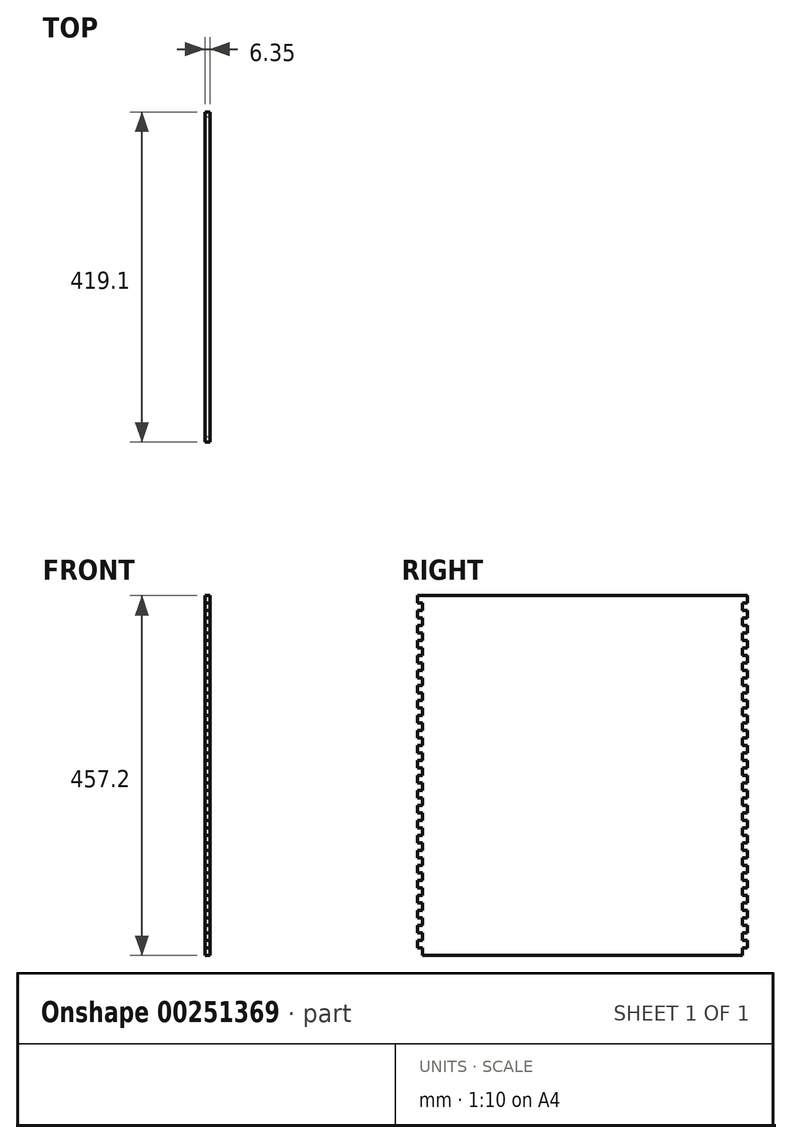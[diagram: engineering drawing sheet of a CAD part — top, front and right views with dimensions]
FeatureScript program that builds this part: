
annotation { "Feature Type Name" : "Feature", "Feature Type Description" : "" }
export const myFeature = defineFeature(function(context is Context, id is Id, definition is map)
    precondition{}
    {
        {
            var Q0;
            Q0=qCreatedBy(makeId("Right.planeOp"),FACE);
            var sketch = newSketch(context, id + "F0", { "sketchPlane" : qUnion([Q0])});
            skLineSegment(sketch, "E0.bottom", {"start": v(-209.55, 228.6) * mm, "end": v(209.55, 228.6) * mm});
            skLineSegment(sketch, "E0.top", {"start": v(-203.2, -228.6) * mm, "end": v(203.2, -228.6) * mm});
            skPoint(sketch, "E0.middle", {"position": v(0, 0) * mm});
            skLineSegment(sketch, "E1.top", {"start": v(-209.55, -219.08) * mm, "end": v(-203.2, -219.08) * mm});
            skLineSegment(sketch, "E1.right", {"start": v(-203.2, -228.6) * mm, "end": v(-203.2, -219.08) * mm});
            skPoint(sketch, "E2.orphan", {"position": v(-215.9, -228.6) * mm});
            skLineSegment(sketch, "E3", {"start": v(-209.55, -219.08) * mm, "end": v(-209.55, -209.55) * mm});
            skLineSegment(sketch, "E4", {"start": v(-209.55, -209.55) * mm, "end": v(-203.2, -209.55) * mm});
            skLineSegment(sketch, "E5.0.1.0", {"start": v(-209.55, -190.5) * mm, "end": v(-203.2, -190.5) * mm});
            skLineSegment(sketch, "E5.0.1.1", {"start": v(-209.55, -200.03) * mm, "end": v(-209.55, -190.5) * mm});
            skLineSegment(sketch, "E5.0.1.2", {"start": v(-209.55, -200.03) * mm, "end": v(-203.2, -200.03) * mm});
            skLineSegment(sketch, "E5.0.1.3", {"start": v(-203.2, -209.55) * mm, "end": v(-203.2, -200.03) * mm});
            skLineSegment(sketch, "E5.0.2.0", {"start": v(-209.55, -171.45) * mm, "end": v(-203.2, -171.45) * mm});
            skLineSegment(sketch, "E5.0.2.1", {"start": v(-209.55, -180.98) * mm, "end": v(-209.55, -171.45) * mm});
            skLineSegment(sketch, "E5.0.2.2", {"start": v(-209.55, -180.97) * mm, "end": v(-203.2, -180.97) * mm});
            skLineSegment(sketch, "E5.0.2.3", {"start": v(-203.2, -190.5) * mm, "end": v(-203.2, -180.98) * mm});
            skLineSegment(sketch, "E5.0.3.0", {"start": v(-209.55, -152.4) * mm, "end": v(-203.2, -152.4) * mm});
            skLineSegment(sketch, "E5.0.3.1", {"start": v(-209.55, -161.93) * mm, "end": v(-209.55, -152.4) * mm});
            skLineSegment(sketch, "E5.0.3.2", {"start": v(-209.55, -161.92) * mm, "end": v(-203.2, -161.92) * mm});
            skLineSegment(sketch, "E5.0.3.3", {"start": v(-203.2, -171.45) * mm, "end": v(-203.2, -161.93) * mm});
            skLineSegment(sketch, "E5.0.4.0", {"start": v(-209.55, -133.35) * mm, "end": v(-203.2, -133.35) * mm});
            skLineSegment(sketch, "E5.0.4.1", {"start": v(-209.55, -142.88) * mm, "end": v(-209.55, -133.35) * mm});
            skLineSegment(sketch, "E5.0.4.2", {"start": v(-209.55, -142.87) * mm, "end": v(-203.2, -142.87) * mm});
            skLineSegment(sketch, "E5.0.4.3", {"start": v(-203.2, -152.4) * mm, "end": v(-203.2, -142.88) * mm});
            skLineSegment(sketch, "E5.0.5.0", {"start": v(-209.55, -114.3) * mm, "end": v(-203.2, -114.3) * mm});
            skLineSegment(sketch, "E5.0.5.1", {"start": v(-209.55, -123.83) * mm, "end": v(-209.55, -114.3) * mm});
            skLineSegment(sketch, "E5.0.5.2", {"start": v(-209.55, -123.82) * mm, "end": v(-203.2, -123.82) * mm});
            skLineSegment(sketch, "E5.0.5.3", {"start": v(-203.2, -133.35) * mm, "end": v(-203.2, -123.83) * mm});
            skLineSegment(sketch, "E5.0.6.0", {"start": v(-209.55, -95.25) * mm, "end": v(-203.2, -95.25) * mm});
            skLineSegment(sketch, "E5.0.6.1", {"start": v(-209.55, -104.78) * mm, "end": v(-209.55, -95.25) * mm});
            skLineSegment(sketch, "E5.0.6.2", {"start": v(-209.55, -104.77) * mm, "end": v(-203.2, -104.77) * mm});
            skLineSegment(sketch, "E5.0.6.3", {"start": v(-203.2, -114.3) * mm, "end": v(-203.2, -104.78) * mm});
            skLineSegment(sketch, "E5.0.7.0", {"start": v(-209.55, -76.2) * mm, "end": v(-203.2, -76.2) * mm});
            skLineSegment(sketch, "E5.0.7.1", {"start": v(-209.55, -85.73) * mm, "end": v(-209.55, -76.2) * mm});
            skLineSegment(sketch, "E5.0.7.2", {"start": v(-209.55, -85.72) * mm, "end": v(-203.2, -85.72) * mm});
            skLineSegment(sketch, "E5.0.7.3", {"start": v(-203.2, -95.25) * mm, "end": v(-203.2, -85.73) * mm});
            skLineSegment(sketch, "E5.0.8.0", {"start": v(-209.55, -57.15) * mm, "end": v(-203.2, -57.15) * mm});
            skLineSegment(sketch, "E5.0.8.1", {"start": v(-209.55, -66.68) * mm, "end": v(-209.55, -57.15) * mm});
            skLineSegment(sketch, "E5.0.8.2", {"start": v(-209.55, -66.67) * mm, "end": v(-203.2, -66.67) * mm});
            skLineSegment(sketch, "E5.0.8.3", {"start": v(-203.2, -76.2) * mm, "end": v(-203.2, -66.68) * mm});
            skLineSegment(sketch, "E5.0.9.0", {"start": v(-209.55, -38.1) * mm, "end": v(-203.2, -38.1) * mm});
            skLineSegment(sketch, "E5.0.9.1", {"start": v(-209.55, -47.62) * mm, "end": v(-209.55, -38.1) * mm});
            skLineSegment(sketch, "E5.0.9.2", {"start": v(-209.55, -47.62) * mm, "end": v(-203.2, -47.62) * mm});
            skLineSegment(sketch, "E5.0.9.3", {"start": v(-203.2, -57.15) * mm, "end": v(-203.2, -47.62) * mm});
            skLineSegment(sketch, "E5.0.10.0", {"start": v(-209.55, -19.05) * mm, "end": v(-203.2, -19.05) * mm});
            skLineSegment(sketch, "E5.0.10.1", {"start": v(-209.55, -28.58) * mm, "end": v(-209.55, -19.05) * mm});
            skLineSegment(sketch, "E5.0.10.2", {"start": v(-209.55, -28.57) * mm, "end": v(-203.2, -28.57) * mm});
            skLineSegment(sketch, "E5.0.10.3", {"start": v(-203.2, -38.1) * mm, "end": v(-203.2, -28.58) * mm});
            skLineSegment(sketch, "E5.0.11.0", {"start": v(-209.55, 0) * mm, "end": v(-203.2, 0) * mm});
            skLineSegment(sketch, "E5.0.11.1", {"start": v(-209.55, -9.53) * mm, "end": v(-209.55, 0) * mm});
            skLineSegment(sketch, "E5.0.11.2", {"start": v(-209.55, -9.52) * mm, "end": v(-203.2, -9.52) * mm});
            skLineSegment(sketch, "E5.0.11.3", {"start": v(-203.2, -19.05) * mm, "end": v(-203.2, -9.53) * mm});
            skLineSegment(sketch, "E5.0.12.0", {"start": v(-209.55, 19.05) * mm, "end": v(-203.2, 19.05) * mm});
            skLineSegment(sketch, "E5.0.12.1", {"start": v(-209.55, 9.53) * mm, "end": v(-209.55, 19.05) * mm});
            skLineSegment(sketch, "E5.0.12.2", {"start": v(-209.55, 9.53) * mm, "end": v(-203.2, 9.53) * mm});
            skLineSegment(sketch, "E5.0.12.3", {"start": v(-203.2, 0) * mm, "end": v(-203.2, 9.53) * mm});
            skLineSegment(sketch, "E5.0.13.0", {"start": v(-209.55, 38.1) * mm, "end": v(-203.2, 38.1) * mm});
            skLineSegment(sketch, "E5.0.13.1", {"start": v(-209.55, 28.57) * mm, "end": v(-209.55, 38.1) * mm});
            skLineSegment(sketch, "E5.0.13.2", {"start": v(-209.55, 28.58) * mm, "end": v(-203.2, 28.58) * mm});
            skLineSegment(sketch, "E5.0.13.3", {"start": v(-203.2, 19.05) * mm, "end": v(-203.2, 28.57) * mm});
            skLineSegment(sketch, "E5.0.14.0", {"start": v(-209.55, 57.15) * mm, "end": v(-203.2, 57.15) * mm});
            skLineSegment(sketch, "E5.0.14.1", {"start": v(-209.55, 47.62) * mm, "end": v(-209.55, 57.15) * mm});
            skLineSegment(sketch, "E5.0.14.2", {"start": v(-209.55, 47.63) * mm, "end": v(-203.2, 47.63) * mm});
            skLineSegment(sketch, "E5.0.14.3", {"start": v(-203.2, 38.1) * mm, "end": v(-203.2, 47.62) * mm});
            skLineSegment(sketch, "E5.0.15.0", {"start": v(-209.55, 76.2) * mm, "end": v(-203.2, 76.2) * mm});
            skLineSegment(sketch, "E5.0.15.1", {"start": v(-209.55, 66.67) * mm, "end": v(-209.55, 76.2) * mm});
            skLineSegment(sketch, "E5.0.15.2", {"start": v(-209.55, 66.68) * mm, "end": v(-203.2, 66.68) * mm});
            skLineSegment(sketch, "E5.0.15.3", {"start": v(-203.2, 57.15) * mm, "end": v(-203.2, 66.67) * mm});
            skLineSegment(sketch, "E5.0.16.0", {"start": v(-209.55, 95.25) * mm, "end": v(-203.2, 95.25) * mm});
            skLineSegment(sketch, "E5.0.16.1", {"start": v(-209.55, 85.72) * mm, "end": v(-209.55, 95.25) * mm});
            skLineSegment(sketch, "E5.0.16.2", {"start": v(-209.55, 85.73) * mm, "end": v(-203.2, 85.73) * mm});
            skLineSegment(sketch, "E5.0.16.3", {"start": v(-203.2, 76.2) * mm, "end": v(-203.2, 85.72) * mm});
            skLineSegment(sketch, "E5.0.17.0", {"start": v(-209.55, 114.3) * mm, "end": v(-203.2, 114.3) * mm});
            skLineSegment(sketch, "E5.0.17.1", {"start": v(-209.55, 104.78) * mm, "end": v(-209.55, 114.3) * mm});
            skLineSegment(sketch, "E5.0.17.2", {"start": v(-209.55, 104.78) * mm, "end": v(-203.2, 104.78) * mm});
            skLineSegment(sketch, "E5.0.17.3", {"start": v(-203.2, 95.25) * mm, "end": v(-203.2, 104.78) * mm});
            skLineSegment(sketch, "E5.0.18.0", {"start": v(-209.55, 133.35) * mm, "end": v(-203.2, 133.35) * mm});
            skLineSegment(sketch, "E5.0.18.1", {"start": v(-209.55, 123.83) * mm, "end": v(-209.55, 133.35) * mm});
            skLineSegment(sketch, "E5.0.18.2", {"start": v(-209.55, 123.83) * mm, "end": v(-203.2, 123.83) * mm});
            skLineSegment(sketch, "E5.0.18.3", {"start": v(-203.2, 114.3) * mm, "end": v(-203.2, 123.83) * mm});
            skLineSegment(sketch, "E5.0.19.0", {"start": v(-209.55, 152.4) * mm, "end": v(-203.2, 152.4) * mm});
            skLineSegment(sketch, "E5.0.19.1", {"start": v(-209.55, 142.87) * mm, "end": v(-209.55, 152.4) * mm});
            skLineSegment(sketch, "E5.0.19.2", {"start": v(-209.55, 142.88) * mm, "end": v(-203.2, 142.88) * mm});
            skLineSegment(sketch, "E5.0.19.3", {"start": v(-203.2, 133.35) * mm, "end": v(-203.2, 142.87) * mm});
            skLineSegment(sketch, "E5.0.20.0", {"start": v(-209.55, 171.45) * mm, "end": v(-203.2, 171.45) * mm});
            skLineSegment(sketch, "E5.0.20.1", {"start": v(-209.55, 161.92) * mm, "end": v(-209.55, 171.45) * mm});
            skLineSegment(sketch, "E5.0.20.2", {"start": v(-209.55, 161.93) * mm, "end": v(-203.2, 161.93) * mm});
            skLineSegment(sketch, "E5.0.20.3", {"start": v(-203.2, 152.4) * mm, "end": v(-203.2, 161.92) * mm});
            skLineSegment(sketch, "E5.0.21.0", {"start": v(-209.55, 190.5) * mm, "end": v(-203.2, 190.5) * mm});
            skLineSegment(sketch, "E5.0.21.1", {"start": v(-209.55, 180.97) * mm, "end": v(-209.55, 190.5) * mm});
            skLineSegment(sketch, "E5.0.21.2", {"start": v(-209.55, 180.98) * mm, "end": v(-203.2, 180.98) * mm});
            skLineSegment(sketch, "E5.0.21.3", {"start": v(-203.2, 171.45) * mm, "end": v(-203.2, 180.97) * mm});
            skLineSegment(sketch, "E5.0.22.0", {"start": v(-209.55, 209.55) * mm, "end": v(-203.2, 209.55) * mm});
            skLineSegment(sketch, "E5.0.22.1", {"start": v(-209.55, 200.03) * mm, "end": v(-209.55, 209.55) * mm});
            skLineSegment(sketch, "E5.0.22.2", {"start": v(-209.55, 200.03) * mm, "end": v(-203.2, 200.03) * mm});
            skLineSegment(sketch, "E5.0.22.3", {"start": v(-203.2, 190.5) * mm, "end": v(-203.2, 200.03) * mm});
            skLineSegment(sketch, "E5.0.23.0", {"start": v(-209.55, 228.6) * mm, "end": v(-203.2, 228.6) * mm});
            skLineSegment(sketch, "E5.0.23.1", {"start": v(-209.55, 219.08) * mm, "end": v(-209.55, 228.6) * mm});
            skLineSegment(sketch, "E5.0.23.2", {"start": v(-209.55, 219.08) * mm, "end": v(-203.2, 219.08) * mm});
            skLineSegment(sketch, "E5.0.23.3", {"start": v(-203.2, 209.55) * mm, "end": v(-203.2, 219.08) * mm});
            skLineSegment(sketch, "E5.direction1", {"start": v(-209.55, -209.55) * mm, "end": v(-203.2, -209.55) * mm, "construction": true});
            skLineSegment(sketch, "E5.direction2", {"start": v(-209.55, -200.03) * mm, "end": v(-209.55, -190.5) * mm, "construction": true});
            skLineSegment(sketch, "E6", {"start": v(0, -228.6) * mm, "end": v(0, 256.4) * mm});
            skLineSegment(sketch, "E7.MirrorCS", {"start": v(209.55, -180.98) * mm, "end": v(209.55, -171.45) * mm});
            skLineSegment(sketch, "E8.MirrorCS", {"start": v(209.55, -171.45) * mm, "end": v(203.2, -171.45) * mm});
            skLineSegment(sketch, "E9.MirrorCS", {"start": v(209.55, -200.03) * mm, "end": v(209.55, -190.5) * mm});
            skLineSegment(sketch, "E10.MirrorCS", {"start": v(209.55, -190.5) * mm, "end": v(203.2, -190.5) * mm});
            skLineSegment(sketch, "E11.MirrorCS", {"start": v(209.55, -209.55) * mm, "end": v(203.2, -209.55) * mm});
            skLineSegment(sketch, "E12.MirrorCS", {"start": v(209.55, -180.97) * mm, "end": v(203.2, -180.97) * mm});
            skLineSegment(sketch, "E13.MirrorCS", {"start": v(209.55, -85.72) * mm, "end": v(203.2, -85.72) * mm});
            skLineSegment(sketch, "E14.MirrorCS", {"start": v(209.55, -9.52) * mm, "end": v(203.2, -9.52) * mm});
            skLineSegment(sketch, "E15.MirrorCS", {"start": v(209.55, 66.68) * mm, "end": v(203.2, 66.68) * mm});
            skLineSegment(sketch, "E16.MirrorCS", {"start": v(209.55, 142.88) * mm, "end": v(203.2, 142.88) * mm});
            skLineSegment(sketch, "E17.MirrorCS", {"start": v(209.55, -161.92) * mm, "end": v(203.2, -161.92) * mm});
            skLineSegment(sketch, "E18.MirrorCS", {"start": v(209.55, 104.78) * mm, "end": v(209.55, 114.3) * mm});
            skLineSegment(sketch, "E19.MirrorCS", {"start": v(209.55, 180.97) * mm, "end": v(209.55, 190.5) * mm});
            skLineSegment(sketch, "E20.MirrorCS", {"start": v(209.55, -123.83) * mm, "end": v(209.55, -114.3) * mm});
            skLineSegment(sketch, "E21.MirrorCS", {"start": v(209.55, -47.62) * mm, "end": v(209.55, -38.1) * mm});
            skLineSegment(sketch, "E22.MirrorCS", {"start": v(209.55, 28.57) * mm, "end": v(209.55, 38.1) * mm});
            skLineSegment(sketch, "E23.MirrorCS", {"start": v(209.55, -85.73) * mm, "end": v(209.55, -76.2) * mm});
            skLineSegment(sketch, "E24.MirrorCS", {"start": v(209.55, -9.53) * mm, "end": v(209.55, 0) * mm});
            skLineSegment(sketch, "E25.MirrorCS", {"start": v(209.55, 66.67) * mm, "end": v(209.55, 76.2) * mm});
            skLineSegment(sketch, "E26.MirrorCS", {"start": v(209.55, 142.87) * mm, "end": v(209.55, 152.4) * mm});
            skLineSegment(sketch, "E27.MirrorCS", {"start": v(209.55, -161.93) * mm, "end": v(209.55, -152.4) * mm});
            skLineSegment(sketch, "E28.MirrorCS", {"start": v(209.55, 114.3) * mm, "end": v(203.2, 114.3) * mm});
            skLineSegment(sketch, "E29.MirrorCS", {"start": v(209.55, 190.5) * mm, "end": v(203.2, 190.5) * mm});
            skLineSegment(sketch, "E30.MirrorCS", {"start": v(209.55, -114.3) * mm, "end": v(203.2, -114.3) * mm});
            skLineSegment(sketch, "E31.MirrorCS", {"start": v(209.55, -38.1) * mm, "end": v(203.2, -38.1) * mm});
            skLineSegment(sketch, "E32.MirrorCS", {"start": v(209.55, 38.1) * mm, "end": v(203.2, 38.1) * mm});
            skLineSegment(sketch, "E33.MirrorCS", {"start": v(203.2, -209.55) * mm, "end": v(203.2, -200.03) * mm});
            skLineSegment(sketch, "E34.MirrorCS", {"start": v(209.55, -200.03) * mm, "end": v(203.2, -200.03) * mm});
            skLineSegment(sketch, "E35.MirrorCS", {"start": v(203.2, -95.25) * mm, "end": v(203.2, -85.73) * mm});
            skLineSegment(sketch, "E36.MirrorCS", {"start": v(203.2, -19.05) * mm, "end": v(203.2, -9.53) * mm});
            skLineSegment(sketch, "E37.MirrorCS", {"start": v(209.55, -219.08) * mm, "end": v(209.55, -209.55) * mm});
            skLineSegment(sketch, "E38.MirrorCS", {"start": v(209.55, -219.08) * mm, "end": v(203.2, -219.08) * mm});
            skLineSegment(sketch, "E39.MirrorCS", {"start": v(203.2, 57.15) * mm, "end": v(203.2, 66.67) * mm});
            skLineSegment(sketch, "E40.MirrorCS", {"start": v(209.55, -152.4) * mm, "end": v(203.2, -152.4) * mm});
            skLineSegment(sketch, "E41.MirrorCS", {"start": v(203.2, 133.35) * mm, "end": v(203.2, 142.87) * mm});
            skLineSegment(sketch, "E42.MirrorCS", {"start": v(203.2, -190.5) * mm, "end": v(203.2, -180.98) * mm});
            skLineSegment(sketch, "E43.MirrorCS", {"start": v(209.55, -76.2) * mm, "end": v(203.2, -76.2) * mm});
            skLineSegment(sketch, "E44.MirrorCS", {"start": v(203.2, 0) * mm, "end": v(203.2, 9.53) * mm});
            skLineSegment(sketch, "E45.MirrorCS", {"start": v(203.2, -76.2) * mm, "end": v(203.2, -66.68) * mm});
            skLineSegment(sketch, "E46.MirrorCS", {"start": v(209.55, 0) * mm, "end": v(203.2, 0) * mm});
            skLineSegment(sketch, "E47.MirrorCS", {"start": v(203.2, 76.2) * mm, "end": v(203.2, 85.72) * mm});
            skLineSegment(sketch, "E48.MirrorCS", {"start": v(209.55, 152.4) * mm, "end": v(203.2, 152.4) * mm});
            skLineSegment(sketch, "E49.MirrorCS", {"start": v(209.55, 76.2) * mm, "end": v(203.2, 76.2) * mm});
            skLineSegment(sketch, "E50.MirrorCS", {"start": v(203.2, 152.4) * mm, "end": v(203.2, 161.92) * mm});
            skLineSegment(sketch, "E51.MirrorCS", {"start": v(203.2, -171.45) * mm, "end": v(203.2, -161.93) * mm});
            skLineSegment(sketch, "E52.MirrorCS", {"start": v(203.2, -152.4) * mm, "end": v(203.2, -142.88) * mm});
            skLineSegment(sketch, "E53.MirrorCS", {"start": v(209.55, 104.78) * mm, "end": v(203.2, 104.78) * mm});
            skLineSegment(sketch, "E54.MirrorCS", {"start": v(209.55, 180.98) * mm, "end": v(203.2, 180.98) * mm});
            skLineSegment(sketch, "E55.MirrorCS", {"start": v(203.2, 190.5) * mm, "end": v(203.2, 200.03) * mm});
            skLineSegment(sketch, "E56.MirrorCS", {"start": v(209.55, -66.67) * mm, "end": v(203.2, -66.67) * mm});
            skLineSegment(sketch, "E57.MirrorCS", {"start": v(203.2, -114.3) * mm, "end": v(203.2, -104.78) * mm});
            skLineSegment(sketch, "E58.MirrorCS", {"start": v(203.2, -38.1) * mm, "end": v(203.2, -28.58) * mm});
            skLineSegment(sketch, "E59.MirrorCS", {"start": v(209.55, 9.53) * mm, "end": v(203.2, 9.53) * mm});
            skLineSegment(sketch, "E60.MirrorCS", {"start": v(209.55, 85.73) * mm, "end": v(203.2, 85.73) * mm});
            skLineSegment(sketch, "E61.MirrorCS", {"start": v(203.2, 38.1) * mm, "end": v(203.2, 47.62) * mm});
            skLineSegment(sketch, "E62.MirrorCS", {"start": v(209.55, 161.93) * mm, "end": v(203.2, 161.93) * mm});
            skLineSegment(sketch, "E63.MirrorCS", {"start": v(203.2, 114.3) * mm, "end": v(203.2, 123.83) * mm});
            skLineSegment(sketch, "E64.MirrorCS", {"start": v(209.55, -142.87) * mm, "end": v(203.2, -142.87) * mm});
            skLineSegment(sketch, "E65.MirrorCS", {"start": v(209.55, 123.83) * mm, "end": v(209.55, 133.35) * mm});
            skLineSegment(sketch, "E66.MirrorCS", {"start": v(209.55, 200.03) * mm, "end": v(209.55, 209.55) * mm});
            skLineSegment(sketch, "E67.MirrorCS", {"start": v(209.55, -104.78) * mm, "end": v(209.55, -95.25) * mm});
            skLineSegment(sketch, "E68.MirrorCS", {"start": v(209.55, -123.82) * mm, "end": v(203.2, -123.82) * mm});
            skLineSegment(sketch, "E69.MirrorCS", {"start": v(209.55, -28.58) * mm, "end": v(209.55, -19.05) * mm});
            skLineSegment(sketch, "E70.MirrorCS", {"start": v(209.55, 47.62) * mm, "end": v(209.55, 57.15) * mm});
            skLineSegment(sketch, "E71.MirrorCS", {"start": v(209.55, -47.62) * mm, "end": v(203.2, -47.62) * mm});
            skLineSegment(sketch, "E72.MirrorCS", {"start": v(209.55, 200.03) * mm, "end": v(203.2, 200.03) * mm});
            skLineSegment(sketch, "E73.MirrorCS", {"start": v(209.55, -200.03) * mm, "end": v(209.55, -190.5) * mm, "construction": true});
            skLineSegment(sketch, "E74.MirrorCS", {"start": v(209.55, -66.68) * mm, "end": v(209.55, -57.15) * mm});
            skLineSegment(sketch, "E75.MirrorCS", {"start": v(209.55, -104.77) * mm, "end": v(203.2, -104.77) * mm});
            skLineSegment(sketch, "E76.MirrorCS", {"start": v(209.55, 9.53) * mm, "end": v(209.55, 19.05) * mm});
            skLineSegment(sketch, "E77.MirrorCS", {"start": v(209.55, -28.57) * mm, "end": v(203.2, -28.57) * mm});
            skLineSegment(sketch, "E78.MirrorCS", {"start": v(209.55, 85.72) * mm, "end": v(209.55, 95.25) * mm});
            skLineSegment(sketch, "E79.MirrorCS", {"start": v(209.55, 47.63) * mm, "end": v(203.2, 47.63) * mm});
            skLineSegment(sketch, "E80.MirrorCS", {"start": v(209.55, 123.83) * mm, "end": v(203.2, 123.83) * mm});
            skLineSegment(sketch, "E81.MirrorCS", {"start": v(209.55, 161.92) * mm, "end": v(209.55, 171.45) * mm});
            skLineSegment(sketch, "E82.MirrorCS", {"start": v(209.55, -142.88) * mm, "end": v(209.55, -133.35) * mm});
            skLineSegment(sketch, "E83.MirrorCS", {"start": v(209.55, 28.58) * mm, "end": v(203.2, 28.58) * mm});
            skLineSegment(sketch, "E84.MirrorCS", {"start": v(209.55, 133.35) * mm, "end": v(203.2, 133.35) * mm});
            skLineSegment(sketch, "E85.MirrorCS", {"start": v(209.55, 209.55) * mm, "end": v(203.2, 209.55) * mm});
            skLineSegment(sketch, "E86.MirrorCS", {"start": v(209.55, -19.05) * mm, "end": v(203.2, -19.05) * mm});
            skLineSegment(sketch, "E87.MirrorCS", {"start": v(209.55, -95.25) * mm, "end": v(203.2, -95.25) * mm});
            skLineSegment(sketch, "E88.MirrorCS", {"start": v(209.55, 57.15) * mm, "end": v(203.2, 57.15) * mm});
            skLineSegment(sketch, "E89.MirrorCS", {"start": v(209.55, -209.55) * mm, "end": v(203.2, -209.55) * mm, "construction": true});
            skLineSegment(sketch, "E90.MirrorCS", {"start": v(209.55, -57.15) * mm, "end": v(203.2, -57.15) * mm});
            skLineSegment(sketch, "E91.MirrorCS", {"start": v(209.55, 19.05) * mm, "end": v(203.2, 19.05) * mm});
            skLineSegment(sketch, "E92.MirrorCS", {"start": v(209.55, 95.25) * mm, "end": v(203.2, 95.25) * mm});
            skLineSegment(sketch, "E93.MirrorCS", {"start": v(209.55, 171.45) * mm, "end": v(203.2, 171.45) * mm});
            skLineSegment(sketch, "E94.MirrorCS", {"start": v(209.55, -133.35) * mm, "end": v(203.2, -133.35) * mm});
            skLineSegment(sketch, "E95.MirrorCS", {"start": v(203.2, 95.25) * mm, "end": v(203.2, 104.78) * mm});
            skLineSegment(sketch, "E96.MirrorCS", {"start": v(203.2, -133.35) * mm, "end": v(203.2, -123.83) * mm});
            skLineSegment(sketch, "E97.MirrorCS", {"start": v(203.2, 171.45) * mm, "end": v(203.2, 180.97) * mm});
            skLineSegment(sketch, "E98.MirrorCS", {"start": v(203.2, 19.05) * mm, "end": v(203.2, 28.57) * mm});
            skLineSegment(sketch, "E99.MirrorCS", {"start": v(203.2, -57.15) * mm, "end": v(203.2, -47.62) * mm});
            skLineSegment(sketch, "E100.MirrorCS", {"start": v(209.55, 219.08) * mm, "end": v(203.2, 219.08) * mm});
            skLineSegment(sketch, "E101.MirrorCS", {"start": v(209.55, 219.08) * mm, "end": v(209.55, 228.6) * mm});
            skLineSegment(sketch, "E102.MirrorCS", {"start": v(203.2, 209.55) * mm, "end": v(203.2, 219.08) * mm});
            skLineSegment(sketch, "E103.MirrorCS", {"start": v(209.55, 228.6) * mm, "end": v(203.2, 228.6) * mm});
            skLineSegment(sketch, "E104.MirrorCS", {"start": v(203.2, -228.6) * mm, "end": v(203.2, -219.08) * mm});
            skPoint(sketch, "E105.MirrorP", {"position": v(215.9, -228.6) * mm});
            skPoint(sketch, "E106.orphan", {"position": v(-215.9, 228.6) * mm});
            skPoint(sketch, "E107.orphan", {"position": v(215.9, 228.6) * mm});
            skSolve(sketch);
        }
        {
            var Q0;
            Q0 = qSketchRegion(id + "F0", true);
            extrude(context, id + "F1", {"entities" : qUnion([Q0]), "depth" : 6.35 * mm});
        }
    });
